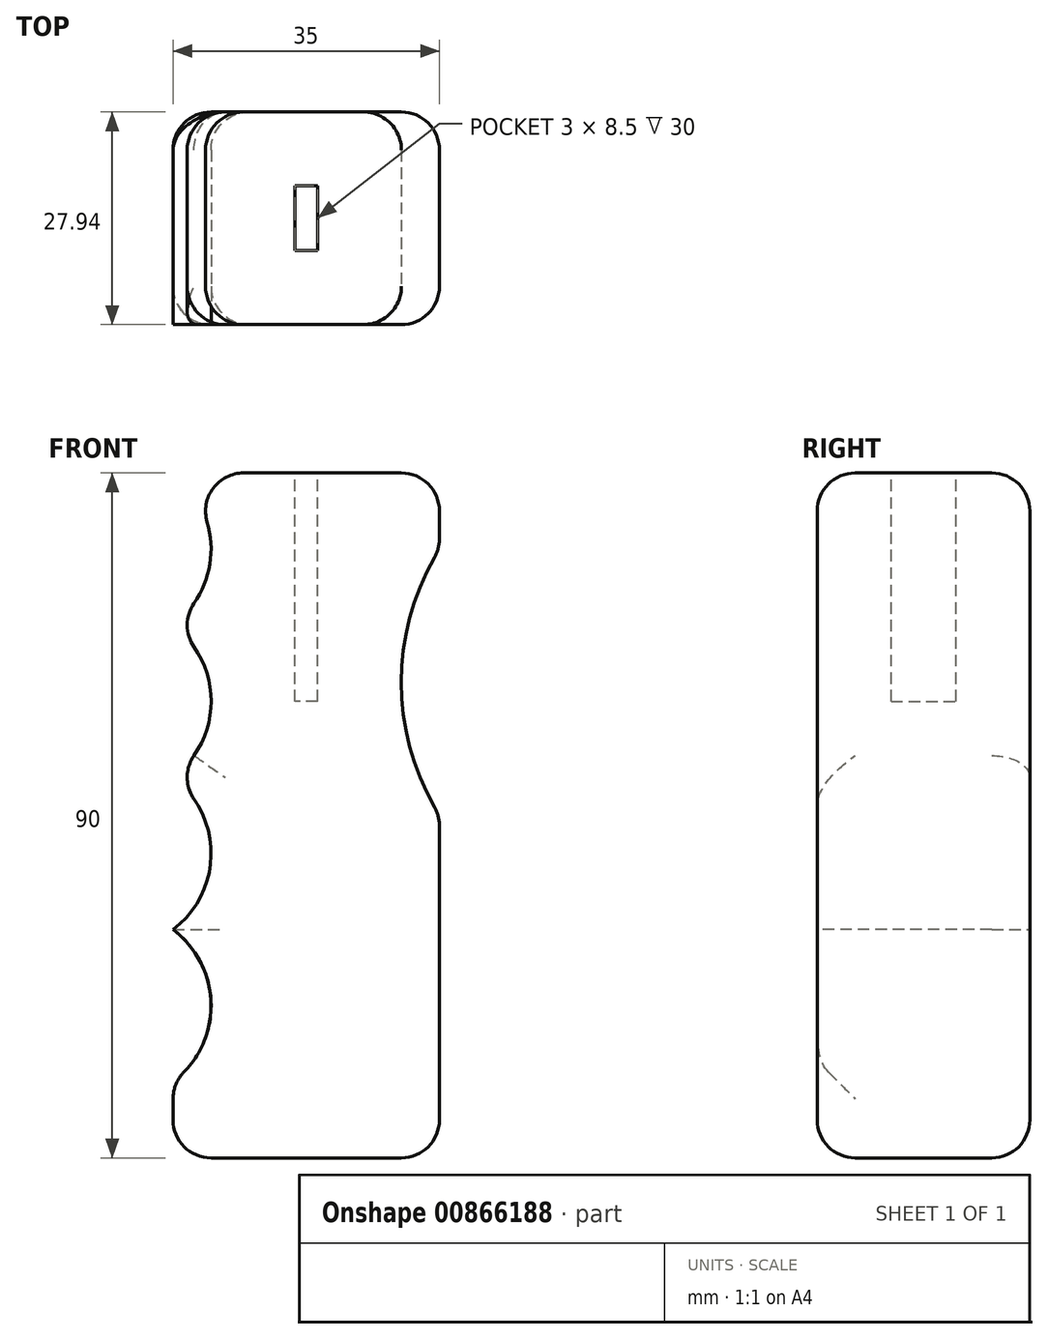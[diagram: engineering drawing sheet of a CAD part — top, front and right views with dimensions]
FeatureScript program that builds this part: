
annotation { "Feature Type Name" : "Feature", "Feature Type Description" : "" }
export const myFeature = defineFeature(function(context is Context, id is Id, definition is map)
    precondition{}
    {
        {
            var Q0;
            Q0=qCreatedBy(makeId("Front.planeOp"),FACE);
            var sketch = newSketch(context, id + "F0", { "sketchPlane" : qUnion([Q0])});
            skLineSegment(sketch, "E0.bottom", {"start": v(35, 90) * mm, "end": v(0, 90) * mm});
            skLineSegment(sketch, "E0.top", {"start": v(35, 0) * mm, "end": v(0, 0) * mm});
            skLineSegment(sketch, "E0.left", {"start": v(35, 90) * mm, "end": v(35, 0) * mm});
            skLineSegment(sketch, "E0.right", {"start": v(0, 90) * mm, "end": v(0, 0) * mm});
            skSolve(sketch);
        }
        {
            var Q0;
            Q0=makeQuery(id+"F0.imprint","IMPRINT",FACE,{"disambiguationData":[TD([[makeQuery(id+"F0.imprint","IMPRINT",EDGE,{"derivedFrom":sQuery(id+"F0.wireOp",EDGE,"E0.bottom")}),1.0]])]});
            extrude(context, id + "F1", {"entities" : qUnion([Q0]), "depth" : 27.94 * mm, "offsetDistance" : 25.4 * mm});
        }
        {
            var Q0;
            Q0=makeQuery(id+"F1.opExtrude","CAP_FACE",FACE,{"disambiguationData":[OSD([sQuery(id+"F0.wireOp",EDGE,"E0.bottom"),sQuery(id+"F0.wireOp",EDGE,"E0.top"),sQuery(id+"F0.wireOp",EDGE,"E0.left"),sQuery(id+"F0.wireOp",EDGE,"E0.right")])],"isStart":false});
            var sketch = newSketch(context, id + "F2", { "sketchPlane" : qUnion([Q0])});
            skArc(sketch, "E1", {"start": v(35, 80) * mm, "mid": v(30, 62.5) * mm, "end": v(35, 45) * mm});
            skArc(sketch, "E2", {"start": v(0, 70) * mm, "mid": v(5, 80) * mm, "end": v(0, 90) * mm});
            skArc(sketch, "E3", {"start": v(0, 50) * mm, "mid": v(5, 60) * mm, "end": v(0, 70) * mm});
            skArc(sketch, "E4", {"start": v(0, 30) * mm, "mid": v(5, 40) * mm, "end": v(0, 50) * mm});
            skArc(sketch, "E5", {"start": v(0, 10) * mm, "mid": v(5, 20) * mm, "end": v(0, 30) * mm});
            skSolve(sketch);
        }
        {
            var Q0;
            Q0=makeQuery(id+"F2.imprint","IMPRINT",FACE,{"disambiguationData":[TD([[makeQuery(id+"F2.imprint","IMPRINT",EDGE,{"derivedFrom":sQuery(id+"F2.wireOp",EDGE,"E1")}),1.0]])]});
            var Q1;
            {var subQ0=sQuery(id+"F2.wireOp",EDGE,"E2");Q1=makeQuery(id+"F2.imprint","IMPRINT",FACE,{"disambiguationData":[TD([[makeQuery(id+"F2.imprint","IMPRINT",EDGE,{"derivedFrom":subQ0}),1.0]])]});}
            var Q2;
            {var subQ0=sQuery(id+"F2.wireOp",EDGE,"E3");Q2=makeQuery(id+"F2.imprint","IMPRINT",FACE,{"disambiguationData":[TD([[makeQuery(id+"F2.imprint","IMPRINT",EDGE,{"derivedFrom":subQ0}),1.0]])]});}
            var Q3;
            {var subQ0=sQuery(id+"F2.wireOp",EDGE,"E4");var subQ1=makeQuery(id+"F1.opExtrude","CAP_EDGE",EDGE,{"disambiguationData":[OSD([sQuery(id+"F0.wireOp",EDGE,"E0.right")])],"isStart":false});var subQ3=makeQuery(id+"F2.imprint","INTERSECT",VERTEX,{"derivedFrom":[subQ1,subQ0]});Q3=makeQuery(id+"F2.imprint","IMPRINT",FACE,{"disambiguationData":[TD([[makeQuery(id+"F2.imprint","IMPRINT",EDGE,{"disambiguationData":[TD([[subQ3,-1.0]])],"derivedFrom":subQ0}),1.0]])]});}
            var Q4;
            {var subQ0=sQuery(id+"F2.wireOp",EDGE,"E5");var subQ1=makeQuery(id+"F1.opExtrude","CAP_EDGE",EDGE,{"disambiguationData":[OSD([sQuery(id+"F0.wireOp",EDGE,"E0.right")])],"isStart":false});var subQ2=makeQuery(id+"F2.imprint","INTERSECT",VERTEX,{"disambiguationData":[OD(0.0)],"derivedFrom":[subQ1,subQ0]});Q4=makeQuery(id+"F2.imprint","IMPRINT",FACE,{"disambiguationData":[TD([[makeQuery(id+"F2.imprint","IMPRINT",EDGE,{"disambiguationData":[TD([[subQ2,-1.0]])],"derivedFrom":subQ0}),1.0]])]});}
            extrude(context, id + "F3", {"entities" : qUnion([Q0, Q1, Q2, Q3, Q4]), "operationType" : NewBodyOperationType.REMOVE, "endBound" : BoundingType.THROUGH_ALL, "oppositeDirection" : true, "depth" : 25.4 * mm, "offsetDistance" : 25.4 * mm});
        }
        {
            var Q0;
            Q0=makeQuery(id+"F1.opExtrude","SWEPT_FACE",FACE,{"disambiguationData":[OSD([sQuery(id+"F0.wireOp",EDGE,"E0.bottom")])]});
            var sketch = newSketch(context, id + "F4", { "sketchPlane" : qUnion([Q0])});
            skLineSegment(sketch, "E6.bottom", {"start": v(19, -18.22) * mm, "end": v(16, -18.22) * mm});
            skLineSegment(sketch, "E6.top", {"start": v(19, -9.72) * mm, "end": v(16, -9.72) * mm});
            skLineSegment(sketch, "E6.left", {"start": v(19, -18.22) * mm, "end": v(19, -9.72) * mm});
            skLineSegment(sketch, "E6.right", {"start": v(16, -18.22) * mm, "end": v(16, -9.72) * mm});
            skPoint(sketch, "E7.0", {"position": v(0, -13.97) * mm});
            skPoint(sketch, "E8.0", {"position": v(17.5, -27.94) * mm});
            skPoint(sketch, "E9.endSnap0", {"position": v(17.5, -18.22) * mm});
            skPoint(sketch, "E9.endSnap1", {"position": v(16, -13.97) * mm});
            skPoint(sketch, "E10", {"position": v(17.5, -13.97) * mm});
            skSolve(sketch);
        }
        {
            var Q0;
            Q0=makeQuery(id+"F4.imprint","IMPRINT",FACE,{"disambiguationData":[TD([[makeQuery(id+"F4.imprint","IMPRINT",EDGE,{"derivedFrom":sQuery(id+"F4.wireOp",EDGE,"E6.bottom")}),-1.0]])]});
            extrude(context, id + "F5", {"entities" : qUnion([Q0]), "operationType" : NewBodyOperationType.REMOVE, "oppositeDirection" : true, "depth" : 30 * mm, "offsetDistance" : 25.4 * mm});
        }
        {
            var Q0;
            Q0=makeQuery(id+"F3.boolean.opBoolean","COPY",FACE,{"derivedFrom":makeQuery(id+"F3.opExtrude","SWEPT_FACE",FACE,{"disambiguationData":[OSD([sQuery(id+"F2.wireOp",EDGE,"E3")])]})});
            var Q1;
            Q1=makeQuery(id+"F3.boolean.opBoolean","COPY",FACE,{"derivedFrom":makeQuery(id+"F3.opExtrude","SWEPT_FACE",FACE,{"disambiguationData":[OSD([sQuery(id+"F2.wireOp",EDGE,"E2")])]})});
            var Q2;
            Q2=makeQuery(id+"F3.boolean.opBoolean","INTERSECT",EDGE,{"derivedFrom":[makeQuery(id+"F1.opExtrude","CAP_FACE",FACE,{"disambiguationData":[OSD([sQuery(id+"F0.wireOp",EDGE,"E0.bottom"),sQuery(id+"F0.wireOp",EDGE,"E0.top"),sQuery(id+"F0.wireOp",EDGE,"E0.left"),sQuery(id+"F0.wireOp",EDGE,"E0.right")])],"isStart":true}),makeQuery(id+"F3.opExtrude","SWEPT_FACE",FACE,{"disambiguationData":[OSD([sQuery(id+"F2.wireOp",EDGE,"E4")])]})]});
            var Q3;
            Q3=makeQuery(id+"F3.boolean.opBoolean","COPY",EDGE,{"derivedFrom":makeQuery(id+"F3.opExtrude","CAP_EDGE",EDGE,{"disambiguationData":[OSD([sQuery(id+"F2.wireOp",EDGE,"E4")])],"isStart":true})});
            var Q4;
            {var subQ0=sQuery(id+"F0.wireOp",EDGE,"E0.right");var subQ2=sQuery(id+"F0.wireOp",EDGE,"E0.top");Q4=makeQuery(id+"F3.boolean.opBoolean","SPLIT",FACE,{"disambiguationData":[TD([makeQuery(id+"F1.opExtrude","SWEPT_FACE",FACE,{"disambiguationData":[OSD([subQ2])]})])],"derivedFrom":makeQuery(id+"F1.opExtrude","SWEPT_FACE",FACE,{"disambiguationData":[OSD([subQ0])]})});}
            var Q5;
            Q5=makeQuery(id+"F1.opExtrude","SWEPT_FACE",FACE,{"disambiguationData":[OSD([sQuery(id+"F0.wireOp",EDGE,"E0.top")])]});
            var Q6;
            {var subQ1=sQuery(id+"F0.wireOp",EDGE,"E0.left");var subQ2=sQuery(id+"F0.wireOp",EDGE,"E0.top");Q6=makeQuery(id+"F3.boolean.opBoolean","SPLIT",FACE,{"disambiguationData":[TD([makeQuery(id+"F1.opExtrude","SWEPT_FACE",FACE,{"disambiguationData":[OSD([subQ2])]})])],"derivedFrom":makeQuery(id+"F1.opExtrude","SWEPT_FACE",FACE,{"disambiguationData":[OSD([subQ1])]})});}
            var Q7;
            Q7=makeQuery(id+"F3.boolean.opBoolean","COPY",FACE,{"derivedFrom":makeQuery(id+"F3.opExtrude","SWEPT_FACE",FACE,{"disambiguationData":[OSD([sQuery(id+"F2.wireOp",EDGE,"E1")])]})});
            var Q8;
            {var subQ0=sQuery(id+"F0.wireOp",EDGE,"E0.bottom");var subQ2=sQuery(id+"F0.wireOp",EDGE,"E0.left");Q8=makeQuery(id+"F3.boolean.opBoolean","SPLIT",FACE,{"disambiguationData":[TD([makeQuery(id+"F1.opExtrude","SWEPT_FACE",FACE,{"disambiguationData":[OSD([subQ0])]})])],"derivedFrom":makeQuery(id+"F1.opExtrude","SWEPT_FACE",FACE,{"disambiguationData":[OSD([subQ2])]})});}
            var Q9;
            Q9=makeQuery(id+"F1.opExtrude","CAP_EDGE",EDGE,{"disambiguationData":[OSD([sQuery(id+"F0.wireOp",EDGE,"E0.bottom")])],"isStart":true});
            var Q10;
            Q10=makeQuery(id+"F1.opExtrude","CAP_EDGE",EDGE,{"disambiguationData":[OSD([sQuery(id+"F0.wireOp",EDGE,"E0.bottom")])],"isStart":false});
            var Q11;
            {var subQ0=sQuery(id+"F2.wireOp",EDGE,"E5");var subQ1=sQuery(id+"F0.wireOp",EDGE,"E0.right");Q11=makeQuery(id+"F3.boolean.opBoolean","COPY",EDGE,{"derivedFrom":makeQuery(id+"F3.opExtrude","SWEPT_EDGE",EDGE,{"disambiguationData":[OSD([subQ1,subQ0]),TDD([makeQuery(id+"F2.imprint","INTERSECT",VERTEX,{"disambiguationData":[OD(1.0)],"derivedFrom":[makeQuery(id+"F1.opExtrude","CAP_EDGE",EDGE,{"disambiguationData":[OSD([subQ1])],"isStart":false}),subQ0]})])]})});}
            var Q12;
            Q12=makeQuery(id+"F3.boolean.opBoolean","COPY",EDGE,{"derivedFrom":makeQuery(id+"F3.opExtrude","CAP_EDGE",EDGE,{"disambiguationData":[OSD([sQuery(id+"F2.wireOp",EDGE,"E5")])],"isStart":true})});
            var Q13;
            Q13=makeQuery(id+"F3.boolean.opBoolean","INTERSECT",EDGE,{"derivedFrom":[makeQuery(id+"F1.opExtrude","CAP_FACE",FACE,{"disambiguationData":[OSD([sQuery(id+"F0.wireOp",EDGE,"E0.bottom"),sQuery(id+"F0.wireOp",EDGE,"E0.top"),sQuery(id+"F0.wireOp",EDGE,"E0.left"),sQuery(id+"F0.wireOp",EDGE,"E0.right")])],"isStart":true}),makeQuery(id+"F3.opExtrude","SWEPT_FACE",FACE,{"disambiguationData":[OSD([sQuery(id+"F2.wireOp",EDGE,"E5")])]})]});
            var Q14;
            {var subQ0=sQuery(id+"F2.wireOp",EDGE,"E5");var subQ1=sQuery(id+"F2.wireOp",EDGE,"E4");var subQ2=sQuery(id+"F0.wireOp",EDGE,"E0.right");Q14=makeQuery(id+"F3.boolean.opBoolean","TWEAK_EDGE",EDGE,{"derivedFrom":[makeQuery(id+"F3.opExtrude","SWEPT_EDGE",EDGE,{"disambiguationData":[OSD([subQ2,subQ1,subQ0]),OD(0.0)]}),makeQuery(id+"F3.opExtrude","SWEPT_EDGE",EDGE,{"disambiguationData":[OSD([subQ2,subQ1,subQ0]),OD(1.0)]})]});}
            fillet(context, id + "F6", {"entities" : qUnion([Q0, Q1, Q2, Q3, Q4, Q5, Q6, Q7, Q8, Q9, Q10, Q11, Q12, Q13, Q14]), "radius" : 5 * mm, "tangentPropagation" : true, "allowEdgeOverflow" : false});
        }
    });
